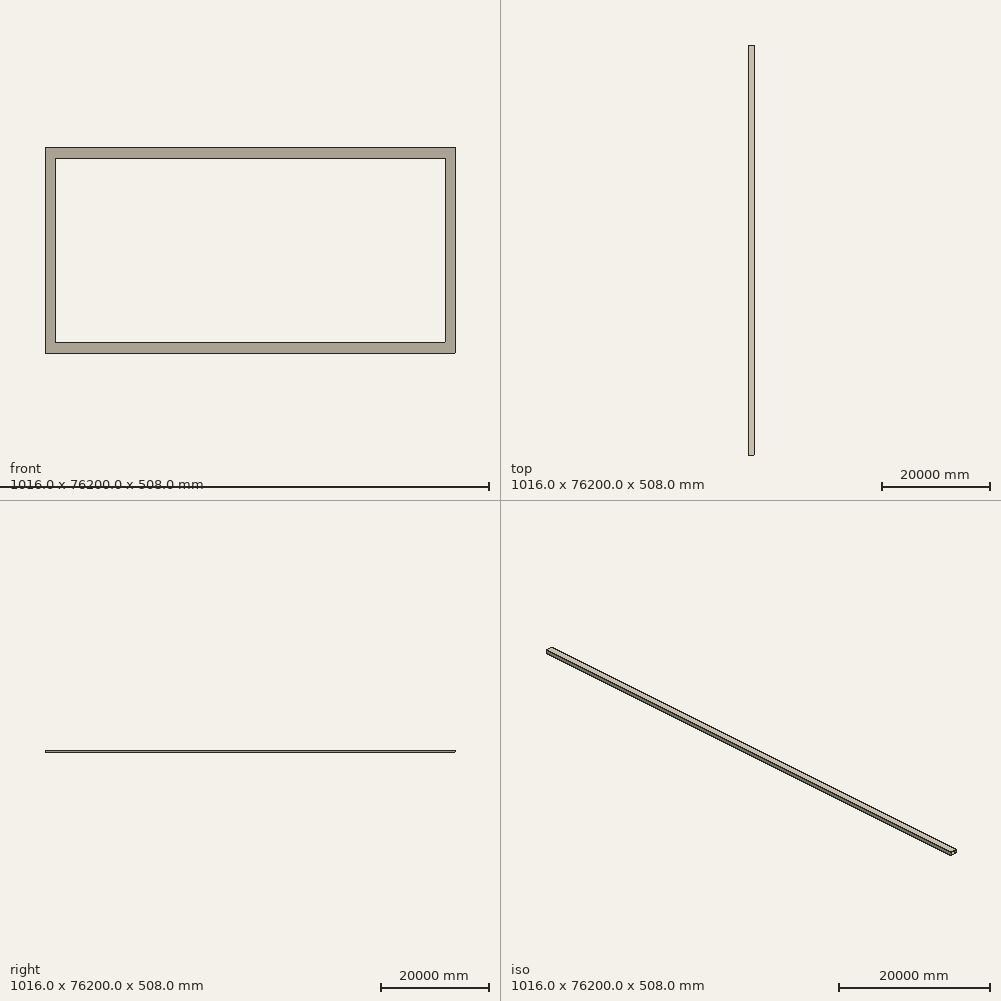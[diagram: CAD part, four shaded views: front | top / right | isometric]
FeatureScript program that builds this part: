
annotation { "Feature Type Name" : "Feature", "Feature Type Description" : "" }
export const myFeature = defineFeature(function(context is Context, id is Id, definition is map)
    precondition{}
    {
        {
            var Q0;
            Q0=qCreatedBy(makeId("Front.planeOp"),FACE);
            var sketch = newSketch(context, id + "F0", { "sketchPlane" : qUnion([Q0])});
            skLineSegment(sketch, "E0.bottom", {"start": v(0, 0) * mm, "end": v(-1016, 0) * mm});
            skLineSegment(sketch, "E0.top", {"start": v(0, 508) * mm, "end": v(-1016, 508) * mm});
            skLineSegment(sketch, "E0.left", {"start": v(0, 0) * mm, "end": v(0, 508) * mm});
            skLineSegment(sketch, "E0.right", {"start": v(-1016, 0) * mm, "end": v(-1016, 508) * mm});
            skLineSegment(sketch, "E1.bottom", {"start": v(-990.6, 25.4) * mm, "end": v(-25.4, 25.4) * mm});
            skLineSegment(sketch, "E1.top", {"start": v(-990.6, 482.6) * mm, "end": v(-25.4, 482.6) * mm});
            skLineSegment(sketch, "E1.left", {"start": v(-990.6, 25.4) * mm, "end": v(-990.6, 482.6) * mm});
            skLineSegment(sketch, "E1.right", {"start": v(-25.4, 25.4) * mm, "end": v(-25.4, 482.6) * mm});
            skSolve(sketch);
        }
        {
            var Q0;
            Q0=qCreatedBy(makeId("Right.planeOp"),FACE);
            var sketch = newSketch(context, id + "F1", { "sketchPlane" : qUnion([Q0])});
            skLineSegment(sketch, "E2", {"start": v(0, 0) * mm, "end": v(76200, 0) * mm});
            skSolve(sketch);
        }
        {
            var Q0;
            Q0 = qSketchRegion(id + "F0", true);
            var Q1;
            Q1 = qConstructionFilter(qBodyType(qCreatedBy(id + "F1" ,EDGE), BodyType.WIRE), ConstructionObject.NO);
            sweep(context, id + "F2", {"profiles" : qUnion([Q0]), "path" : qUnion([Q1])});
        }
    });
